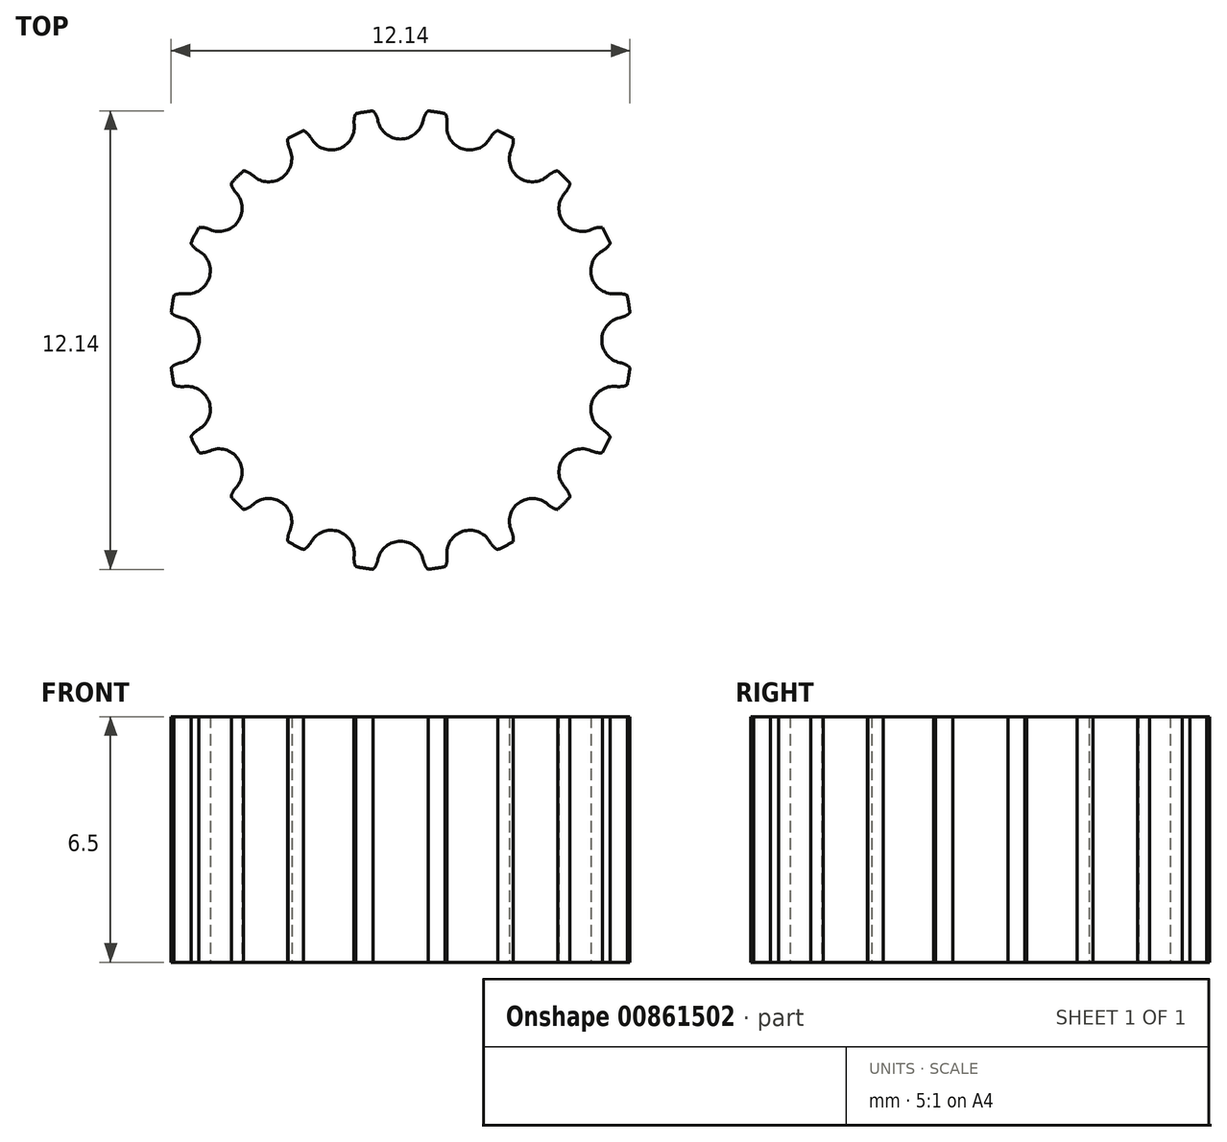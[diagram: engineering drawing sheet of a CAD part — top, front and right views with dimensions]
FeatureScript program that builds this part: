
annotation { "Feature Type Name" : "Feature", "Feature Type Description" : "" }
export const myFeature = defineFeature(function(context is Context, id is Id, definition is map)
    precondition{}
    {
        {
            assignVariable(context, id + "F0", {"name" : "Teeth", "anyValue" : 20});
        }
        {
            var Q0;
            Q0=qCreatedBy(makeId("Top.planeOp"),FACE);
            var sketch = newSketch(context, id + "F1", { "sketchPlane" : qUnion([Q0])});
            skCircle(sketch, "E0", {"center": v(0, 0) * mm, "radius": 6.11 * mm});
            skSolve(sketch);
        }
        {
            var Q0;
            Q0=qCreatedBy(makeId("Top.planeOp"),FACE);
            var sketch = newSketch(context, id + "F2", { "sketchPlane" : qUnion([Q0])});
            skArc(sketch, "E1.0", {"start": v(0.73, 6.07) * mm, "mid": v(0, 6.11) * mm, "end": v(-0.73, 6.07) * mm});
            skLineSegment(sketch, "E2", {"start": v(0, 0) * mm, "end": v(0, 5.93) * mm, "construction": true});
            skArc(sketch, "E3", {"start": v(0, 5.32) * mm, "mid": v(-0.38, 5.46) * mm, "end": v(-0.6, 5.8) * mm});
            skArc(sketch, "E4", {"start": v(-0.6, 5.8) * mm, "mid": v(-0.63, 5.91) * mm, "end": v(-0.67, 6) * mm});
            skArc(sketch, "E5", {"start": v(-0.67, 6) * mm, "mid": v(-0.7, 6.04) * mm, "end": v(-0.73, 6.07) * mm});
            skArc(sketch, "E6.MirrorCS", {"start": v(0, 5.32) * mm, "mid": v(0.38, 5.46) * mm, "end": v(0.6, 5.8) * mm});
            skArc(sketch, "E7.MirrorCS", {"start": v(0.67, 6) * mm, "mid": v(0.7, 6.04) * mm, "end": v(0.73, 6.07) * mm});
            skArc(sketch, "E8.MirrorCS", {"start": v(0.6, 5.8) * mm, "mid": v(0.63, 5.91) * mm, "end": v(0.67, 6) * mm});
            skSolve(sketch);
        }
        {
            var Q0;
            Q0=qSketchRegion(id+"F1",true);
            extrude(context, id + "F3", {"entities" : qUnion([Q0]), "depth" : 6.5 * mm, "offsetDistance" : 25 * mm});
        }
        {
            var Q0;
            Q0=makeQuery(id+"F2.imprint","IMPRINT",FACE,{"disambiguationData":[TD([[makeQuery(id+"F2.imprint","IMPRINT",EDGE,{"derivedFrom":sQuery(id+"F2.wireOp",EDGE,"E1.0")}),1.0]])]});
            extrude(context, id + "F4", {"entities" : qUnion([Q0]), "depth" : 25 * mm, "offsetDistance" : 25 * mm});
        }
        {
            var Q0;
            Q0=makeQuery(id+"F4.opExtrude","SWEPT_BODY",BODY,{"disambiguationData":[OSD([sQuery(id+"F2.wireOp",EDGE,"E1.0"),sQuery(id+"F2.wireOp",EDGE,"E3"),sQuery(id+"F2.wireOp",EDGE,"E4"),sQuery(id+"F2.wireOp",EDGE,"E5"),sQuery(id+"F2.wireOp",EDGE,"E6.MirrorCS"),sQuery(id+"F2.wireOp",EDGE,"E7.MirrorCS"),sQuery(id+"F2.wireOp",EDGE,"E8.MirrorCS")])]});
            var Q1;
            Q1=sQuery(id+"F1.wireOp",EDGE,"E0");
            circularPattern(context, id + "F5", {"operationType" : NewBodyOperationType.REMOVE, "entities" : qUnion([Q0]), "axis" : qUnion([Q1]), "angle" : 360 * degree, "instanceCount" : getVariable(context, 'Teeth'), "equalSpace" : true});
        }
    });
